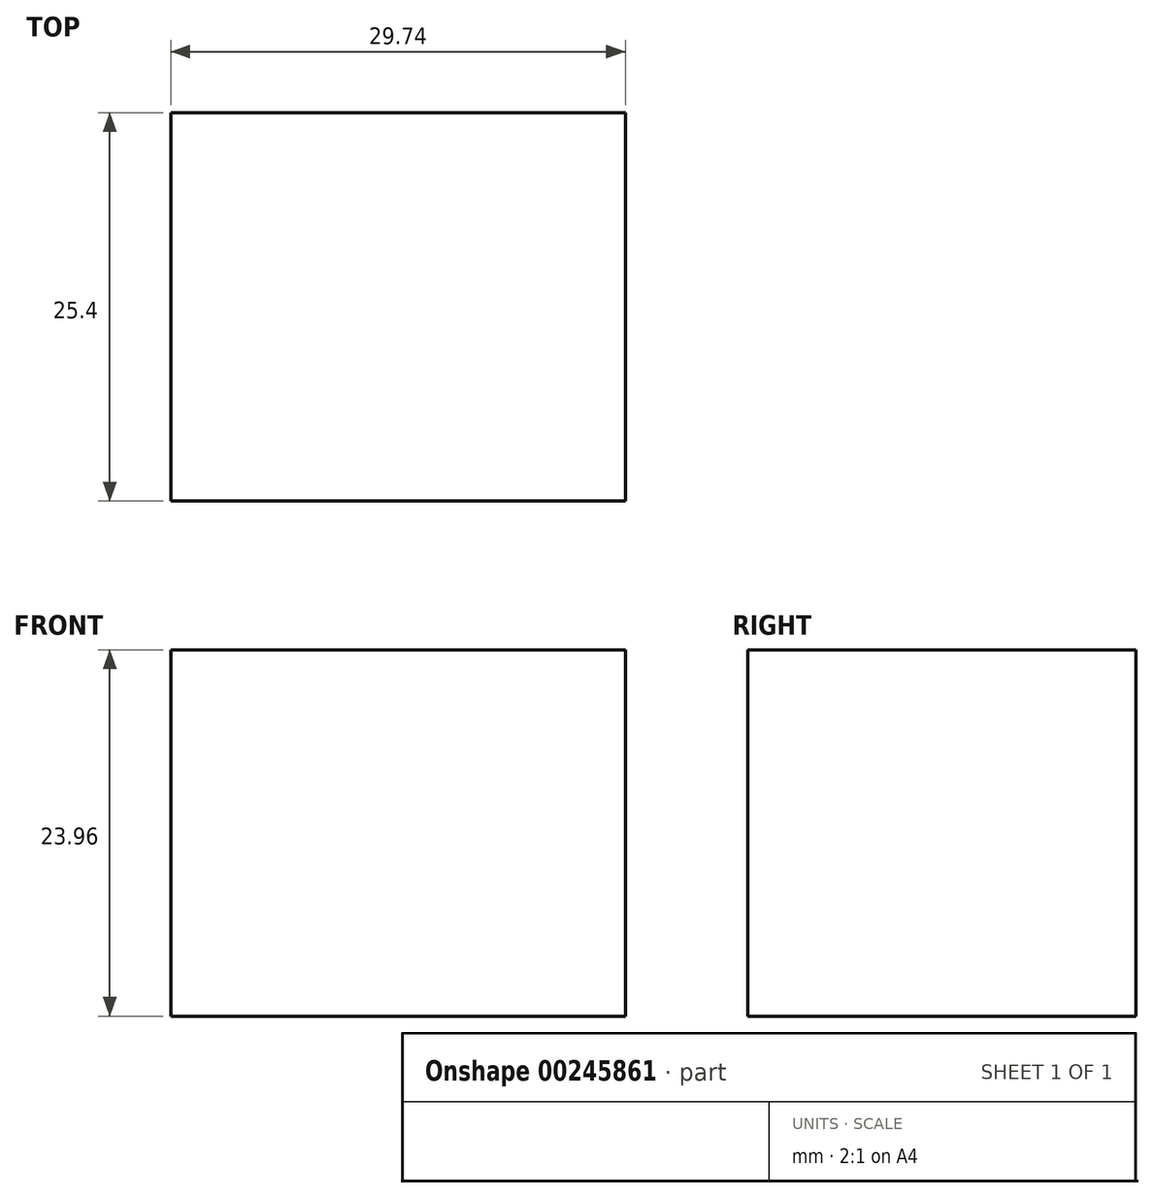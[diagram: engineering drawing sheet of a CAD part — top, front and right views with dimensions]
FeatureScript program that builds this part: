
annotation { "Feature Type Name" : "Feature", "Feature Type Description" : "" }
export const myFeature = defineFeature(function(context is Context, id is Id, definition is map)
    precondition{}
    {
        {
            var Q0;
            Q0=qCreatedBy(makeId("Front.planeOp"),FACE);
            var sketch = newSketch(context, id + "F0", { "sketchPlane" : qUnion([Q0])});
            skLineSegment(sketch, "E0.bottom", {"start": v(14.87, 11.98) * mm, "end": v(-14.87, 11.98) * mm});
            skLineSegment(sketch, "E0.top", {"start": v(14.87, -11.98) * mm, "end": v(-14.87, -11.98) * mm});
            skLineSegment(sketch, "E0.left", {"start": v(14.87, 11.98) * mm, "end": v(14.87, -11.98) * mm});
            skLineSegment(sketch, "E0.right", {"start": v(-14.87, 11.98) * mm, "end": v(-14.87, -11.98) * mm});
            skPoint(sketch, "E0.middle", {"position": v(0, 0) * mm});
            skLineSegment(sketch, "E1", {"start": v(0, 0) * mm, "end": v(0, 41.41) * mm});
            skPoint(sketch, "E1.endSnap0", {"position": v(0, 11.98) * mm});
            skLineSegment(sketch, "E2", {"start": v(0, 41.41) * mm, "end": v(-28.82, 63.56) * mm});
            skLineSegment(sketch, "E3", {"start": v(-28.82, 63.56) * mm, "end": v(-45.81, 51.12) * mm});
            skSolve(sketch);
        }
        {
            var Q0;
            Q0 = qSketchRegion(id + "F0", true);
            extrude(context, id + "F1", {"entities" : qUnion([Q0]), "depth" : 25.4 * mm});
        }
    });
